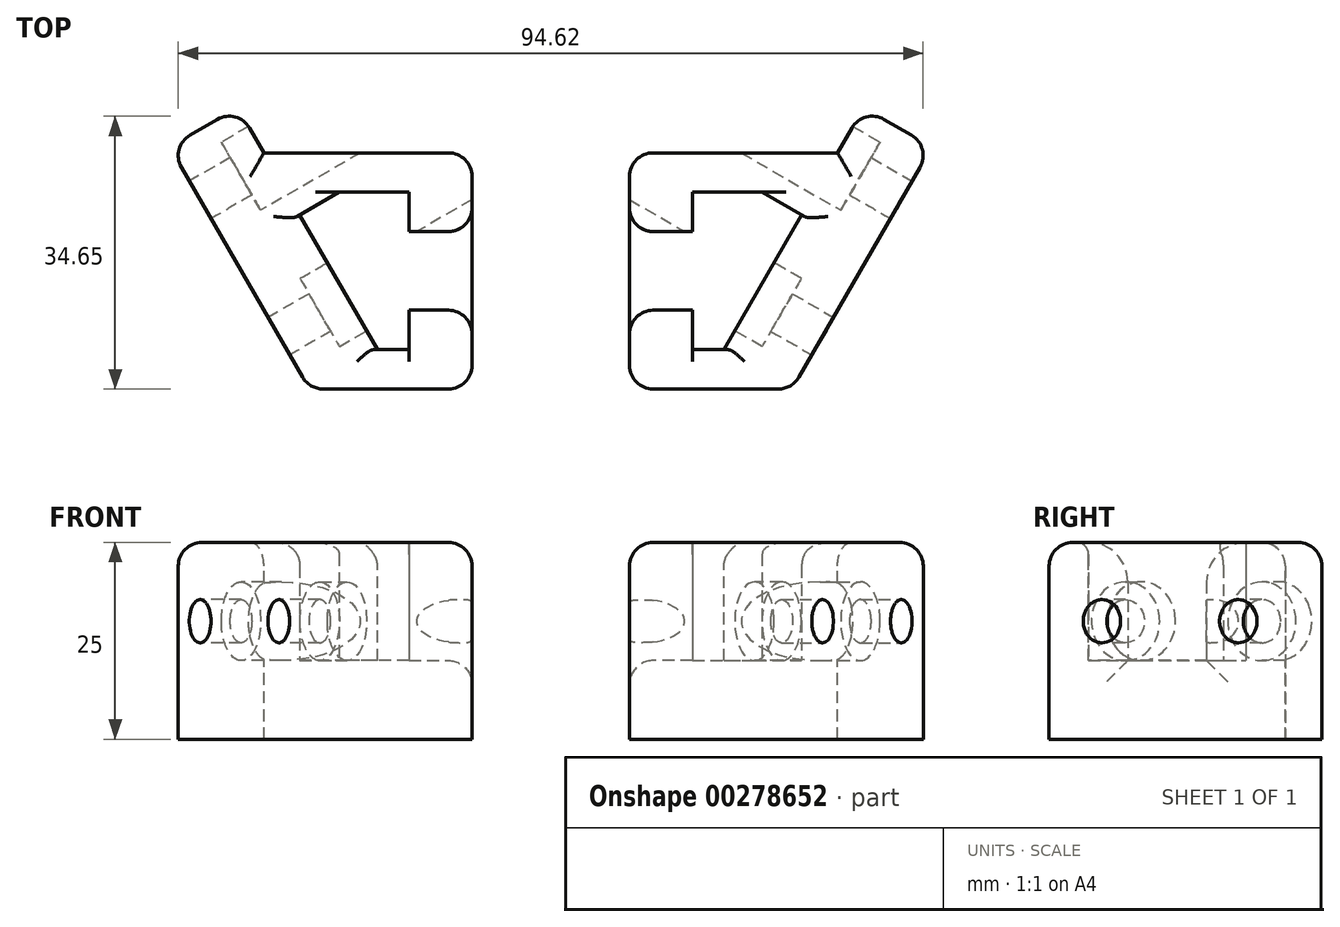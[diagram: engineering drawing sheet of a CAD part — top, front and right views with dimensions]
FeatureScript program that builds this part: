
annotation { "Feature Type Name" : "Feature", "Feature Type Description" : "" }
export const myFeature = defineFeature(function(context is Context, id is Id, definition is map)
    precondition{}
    {
        {
            var Q0;
            Q0=qCreatedBy(makeId("Top.planeOp"),FACE);
            var sketch = newSketch(context, id + "F0", { "sketchPlane" : qUnion([Q0])});
            skLineSegment(sketch, "E0.bottom", {"start": v(-4, 10) * mm, "end": v(4, 10) * mm});
            skLineSegment(sketch, "E0.top", {"start": v(-4, -10) * mm, "end": v(4, -10) * mm});
            skLineSegment(sketch, "E0.left", {"start": v(-4, 10) * mm, "end": v(-4, -10) * mm});
            skLineSegment(sketch, "E0.right", {"start": v(4, 10) * mm, "end": v(4, -10) * mm});
            skPoint(sketch, "E1", {"position": v(0, 10) * mm});
            skPoint(sketch, "E2", {"position": v(4, 0) * mm});
            skLineSegment(sketch, "E3.bottom", {"start": v(-4, 5) * mm, "end": v(4, 5) * mm});
            skLineSegment(sketch, "E3.top", {"start": v(-4, -5) * mm, "end": v(4, -5) * mm});
            skLineSegment(sketch, "E3.left", {"start": v(-4, 5) * mm, "end": v(-4, -5) * mm});
            skLineSegment(sketch, "E3.right", {"start": v(4, 5) * mm, "end": v(4, -5) * mm});
            skPoint(sketch, "E4", {"position": v(-4, 0) * mm});
            skSolve(sketch);
        }
        {
            var Q0;
            {var subQ0=sQuery(id+"F0.wireOp",EDGE,"E0.bottom");Q0=makeQuery(id+"F0.imprint","IMPRINT",FACE,{"disambiguationData":[TD([[makeQuery(id+"F0.imprint","IMPRINT",EDGE,{"derivedFrom":subQ0}),-1.0]])]});}
            var Q1;
            {var subQ0=sQuery(id+"F0.wireOp",EDGE,"E0.top");Q1=makeQuery(id+"F0.imprint","IMPRINT",FACE,{"disambiguationData":[TD([[makeQuery(id+"F0.imprint","IMPRINT",EDGE,{"derivedFrom":subQ0}),1.0]])]});}
            extrude(context, id + "F1", {"entities" : qUnion([Q0, Q1]), "depth" : 25 * mm});
        }
        {
            var Q0;
            Q0=makeQuery(id+"F1.opExtrude","CAP_FACE",FACE,{"disambiguationData":[OSD([sQuery(id+"F0.wireOp",EDGE,"E0.top"),sQuery(id+"F0.wireOp",EDGE,"E0.left"),sQuery(id+"F0.wireOp",EDGE,"E0.right"),sQuery(id+"F0.wireOp",EDGE,"E3.top")])],"isStart":true});
            var sketch = newSketch(context, id + "F2", { "sketchPlane" : qUnion([Q0])});
            skLineSegment(sketch, "E5.bottom", {"start": v(4, -10) * mm, "end": v(-8, -10) * mm});
            skLineSegment(sketch, "E5.top", {"start": v(4, 10) * mm, "end": v(-8, 10) * mm});
            skLineSegment(sketch, "E5.left", {"start": v(4, -10) * mm, "end": v(4, 10) * mm});
            skLineSegment(sketch, "E5.right", {"start": v(-8, -10) * mm, "end": v(-8, 10) * mm});
            skLineSegment(sketch, "E6", {"start": v(-8, 10) * mm, "end": v(-19.55, -10) * mm});
            skLineSegment(sketch, "E7", {"start": v(-8, -10) * mm, "end": v(-19.55, -10) * mm});
            skSolve(sketch);
        }
        {
            var Q0;
            {var subQ4=sQuery(id+"F2.wireOp",EDGE,"E5.bottom");Q0=makeQuery(id+"F2.imprint","IMPRINT",FACE,{"disambiguationData":[TD([[makeQuery(id+"F2.imprint","IMPRINT",EDGE,{"derivedFrom":subQ4}),-1.0]])]});}
            var Q1;
            Q1=makeQuery(id+"F2.imprint","IMPRINT",FACE,{"disambiguationData":[TD([[makeQuery(id+"F2.imprint","IMPRINT",EDGE,{"derivedFrom":sQuery(id+"F2.wireOp",EDGE,"E5.right")}),1.0]])]});
            extrude(context, id + "F3", {"entities" : qUnion([Q0, Q1]), "oppositeDirection" : true, "depth" : 10 * mm});
        }
        {
            var Q0;
            Q0=makeQuery(id+"F3.opExtrude","SWEPT_FACE",FACE,{"disambiguationData":[OSD([sQuery(id+"F2.wireOp",EDGE,"E6")])]});
            var sketch = newSketch(context, id + "F4", { "sketchPlane" : qUnion([Q0])});
            skLineSegment(sketch, "E8.bottom", {"start": v(4.66, 0) * mm, "end": v(-18.43, 0) * mm});
            skLineSegment(sketch, "E8.top", {"start": v(4.66, 25) * mm, "end": v(-18.43, 25) * mm});
            skLineSegment(sketch, "E8.left", {"start": v(4.66, 0) * mm, "end": v(4.66, 25) * mm});
            skLineSegment(sketch, "E8.right", {"start": v(-18.43, 0) * mm, "end": v(-18.43, 25) * mm});
            skSolve(sketch);
        }
        {
            var Q0;
            {var subQ0=sQuery(id+"F4.wireOp",EDGE,"E8.top");Q0=makeQuery(id+"F4.imprint","IMPRINT",FACE,{"disambiguationData":[TD([[makeQuery(id+"F4.imprint","IMPRINT",EDGE,{"derivedFrom":subQ0}),1.0]])]});}
            var Q1;
            {var subQ0=sQuery(id+"F4.wireOp",EDGE,"E8.bottom");Q1=makeQuery(id+"F4.imprint","IMPRINT",FACE,{"disambiguationData":[TD([[makeQuery(id+"F4.imprint","IMPRINT",EDGE,{"derivedFrom":subQ0}),-1.0]])]});}
            extrude(context, id + "F5", {"entities" : qUnion([Q0, Q1]), "operationType" : NewBodyOperationType.ADD, "depth" : 10 * mm});
        }
        {
            var Q0;
            Q0=makeQuery(id+"F1.opExtrude","SWEPT_FACE",FACE,{"disambiguationData":[OSD([sQuery(id+"F0.wireOp",EDGE,"E0.top")])]});
            var sketch = newSketch(context, id + "F6", { "sketchPlane" : qUnion([Q0])});
            skLineSegment(sketch, "E9.bottom", {"start": v(4, 25) * mm, "end": v(-16.66, 25) * mm});
            skLineSegment(sketch, "E9.top", {"start": v(4, 0) * mm, "end": v(-16.66, 0) * mm});
            skLineSegment(sketch, "E9.left", {"start": v(4, 25) * mm, "end": v(4, 0) * mm});
            skLineSegment(sketch, "E9.right", {"start": v(-16.66, 25) * mm, "end": v(-16.66, 0) * mm});
            skSolve(sketch);
        }
        {
            var Q0;
            {var subQ2=sQuery(id+"F6.wireOp",EDGE,"E9.right");Q0=makeQuery(id+"F6.imprint","IMPRINT",FACE,{"disambiguationData":[TD([[makeQuery(id+"F6.imprint","IMPRINT",EDGE,{"derivedFrom":subQ2}),1.0]])]});}
            var Q1;
            {var subQ2=sQuery(id+"F6.wireOp",EDGE,"E9.left");Q1=makeQuery(id+"F6.imprint","IMPRINT",FACE,{"disambiguationData":[TD([[makeQuery(id+"F6.imprint","IMPRINT",EDGE,{"derivedFrom":subQ2}),-1.0]])]});}
            extrude(context, id + "F7", {"entities" : qUnion([Q0, Q1]), "depth" : 2.5 * mm});
        }
        {
            var Q0;
            Q0=makeQuery(id+"F1.opExtrude","SWEPT_FACE",FACE,{"disambiguationData":[OSD([sQuery(id+"F0.wireOp",EDGE,"E0.bottom")])]});
            var sketch = newSketch(context, id + "F8", { "sketchPlane" : qUnion([Q0])});
            skLineSegment(sketch, "E10.bottom", {"start": v(-4, 25) * mm, "end": v(28.2, 25) * mm});
            skLineSegment(sketch, "E10.top", {"start": v(-4, 0) * mm, "end": v(28.2, 0) * mm});
            skLineSegment(sketch, "E10.left", {"start": v(-4, 25) * mm, "end": v(-4, 0) * mm});
            skLineSegment(sketch, "E10.right", {"start": v(28.2, 25) * mm, "end": v(28.2, 0) * mm});
            skSolve(sketch);
        }
        {
            var Q0;
            {var subQ2=sQuery(id+"F8.wireOp",EDGE,"E10.right");Q0=makeQuery(id+"F8.imprint","IMPRINT",FACE,{"disambiguationData":[TD([[makeQuery(id+"F8.imprint","IMPRINT",EDGE,{"derivedFrom":subQ2}),-1.0]])]});}
            var Q1;
            {var subQ2=sQuery(id+"F8.wireOp",EDGE,"E10.left");Q1=makeQuery(id+"F8.imprint","IMPRINT",FACE,{"disambiguationData":[TD([[makeQuery(id+"F8.imprint","IMPRINT",EDGE,{"derivedFrom":subQ2}),1.0]])]});}
            extrude(context, id + "F9", {"entities" : qUnion([Q0, Q1]), "depth" : 5 * mm});
        }
        {
            var Q0;
            Q0=makeQuery(id+"F9.opExtrude","SWEPT_FACE",FACE,{"disambiguationData":[OSD([sQuery(id+"F8.wireOp",EDGE,"E10.bottom")])]});
            var sketch = newSketch(context, id + "F10", { "sketchPlane" : qUnion([Q0])});
            skLineSegment(sketch, "E11", {"start": v(-28.2, 10) * mm, "end": v(-28.2, 5) * mm});
            skLineSegment(sketch, "E12", {"start": v(-28.2, 5) * mm, "end": v(-19.55, 10) * mm});
            skLineSegment(sketch, "E13", {"start": v(-19.55, 10) * mm, "end": v(-28.2, 10) * mm});
            skSolve(sketch);
        }
        {
            var Q0;
            Q0=makeQuery(id+"F10.imprint","IMPRINT",FACE,{"disambiguationData":[TD([[makeQuery(id+"F10.imprint","IMPRINT",EDGE,{"derivedFrom":sQuery(id+"F10.wireOp",EDGE,"E11")}),1.0]])]});
            var Q1;
            Q1=makeQuery(id+"F9.opExtrude","SWEPT_FACE",FACE,{"disambiguationData":[OSD([sQuery(id+"F8.wireOp",EDGE,"E10.top")])]});
            extrude(context, id + "F11", {"entities" : qUnion([Q0]), "endBound" : BoundingType.UP_TO_SURFACE, "oppositeDirection" : true, "endBoundEntityFace" : qUnion([Q1]), "depth" : 25 * mm});
        }
        {
            var Q0;
            Q0=makeQuery(id+"F1.opExtrude","SWEPT_BODY",BODY,{"disambiguationData":[OSD([sQuery(id+"F0.wireOp",EDGE,"E0.bottom"),sQuery(id+"F0.wireOp",EDGE,"E0.left"),sQuery(id+"F0.wireOp",EDGE,"E0.right"),sQuery(id+"F0.wireOp",EDGE,"E3.bottom")])]});
            var Q1;
            Q1=makeQuery(id+"F1.opExtrude","SWEPT_BODY",BODY,{"disambiguationData":[OSD([sQuery(id+"F0.wireOp",EDGE,"E0.top"),sQuery(id+"F0.wireOp",EDGE,"E0.left"),sQuery(id+"F0.wireOp",EDGE,"E0.right"),sQuery(id+"F0.wireOp",EDGE,"E3.top")])]});
            var Q2;
            Q2=makeQuery(id+"F3.opExtrude","SWEPT_BODY",BODY,{"disambiguationData":[OSD([sQuery(id+"F0.wireOp",EDGE,"E0.left"),sQuery(id+"F0.wireOp",EDGE,"E3.top"),sQuery(id+"F2.wireOp",EDGE,"E5.bottom"),sQuery(id+"F2.wireOp",EDGE,"E5.top"),sQuery(id+"F2.wireOp",EDGE,"E5.left"),sQuery(id+"F2.wireOp",EDGE,"E6"),sQuery(id+"F2.wireOp",EDGE,"E7")])]});
            var Q3;
            Q3=makeQuery(id+"F7.opExtrude","SWEPT_BODY",BODY,{"disambiguationData":[OSD([sQuery(id+"F6.wireOp",EDGE,"E9.bottom"),sQuery(id+"F6.wireOp",EDGE,"E9.top"),sQuery(id+"F6.wireOp",EDGE,"E9.left"),sQuery(id+"F6.wireOp",EDGE,"E9.right")])]});
            var Q4;
            Q4=makeQuery(id+"F9.opExtrude","SWEPT_BODY",BODY,{"disambiguationData":[OSD([sQuery(id+"F8.wireOp",EDGE,"E10.bottom"),sQuery(id+"F8.wireOp",EDGE,"E10.top"),sQuery(id+"F8.wireOp",EDGE,"E10.left"),sQuery(id+"F8.wireOp",EDGE,"E10.right")])]});
            var Q5;
            Q5=makeQuery(id+"F11.opExtrude","SWEPT_BODY",BODY,{"disambiguationData":[OSD([sQuery(id+"F10.wireOp",EDGE,"E11"),sQuery(id+"F10.wireOp",EDGE,"E12"),sQuery(id+"F10.wireOp",EDGE,"E13")])]});
            booleanBodies(context, id + "F12", {"operationType" : BooleanOperationType.UNION, "tools" : qUnion([Q0, Q1, Q2, Q3, Q4, Q5])});
        }
        {
            var Q0;
            {var subQ0=sQuery(id+"F0.wireOp",EDGE,"E0.right");var subQ1=sQuery(id+"F0.wireOp",EDGE,"E0.left");Q0=makeQuery(id+"F12.opBoolean","MERGE",FACE,{"derivedFrom":[makeQuery(id+"F1.opExtrude","CAP_FACE",FACE,{"disambiguationData":[OSD([sQuery(id+"F0.wireOp",EDGE,"E0.bottom"),subQ1,subQ0,sQuery(id+"F0.wireOp",EDGE,"E3.bottom")])],"isStart":false}),makeQuery(id+"F1.opExtrude","CAP_FACE",FACE,{"disambiguationData":[OSD([sQuery(id+"F0.wireOp",EDGE,"E0.top"),subQ1,subQ0,sQuery(id+"F0.wireOp",EDGE,"E3.top")])],"isStart":false}),makeQuery(id+"F5.opExtrude","SWEPT_FACE",FACE,{"disambiguationData":[OSD([sQuery(id+"F4.wireOp",EDGE,"E8.top")])]}),makeQuery(id+"F7.opExtrude","SWEPT_FACE",FACE,{"disambiguationData":[OSD([sQuery(id+"F6.wireOp",EDGE,"E9.bottom")])]}),makeQuery(id+"F9.opExtrude","SWEPT_FACE",FACE,{"disambiguationData":[OSD([sQuery(id+"F8.wireOp",EDGE,"E10.bottom")])]}),makeQuery(id+"F11.opExtrude","CAP_FACE",FACE,{"disambiguationData":[OSD([sQuery(id+"F10.wireOp",EDGE,"E11"),sQuery(id+"F10.wireOp",EDGE,"E12"),sQuery(id+"F10.wireOp",EDGE,"E13")])],"isStart":true})]});}
            var sketch = newSketch(context, id + "F13", { "sketchPlane" : qUnion([Q0])});
            skLineSegment(sketch, "E14", {"start": v(-28.2, 5) * mm, "end": v(-32.54, 12.5) * mm});
            skLineSegment(sketch, "E15", {"start": v(-32.54, 12.5) * mm, "end": v(-23.88, 17.5) * mm});
            skLineSegment(sketch, "E16", {"start": v(-23.88, 17.5) * mm, "end": v(-19.55, 10) * mm});
            skLineSegment(sketch, "E17", {"start": v(-28.2, 15) * mm, "end": v(-32.54, 15) * mm});
            skLineSegment(sketch, "E18", {"start": v(-32.54, 15) * mm, "end": v(-32.54, 12.5) * mm});
            skSolve(sketch);
        }
        {
            var Q0;
            {var subQ0=sQuery(id+"F13.wireOp",EDGE,"E14");Q0=makeQuery(id+"F13.imprint","IMPRINT",FACE,{"disambiguationData":[TD([[makeQuery(id+"F13.imprint","IMPRINT",EDGE,{"derivedFrom":subQ0}),-1.0]])]});}
            var Q1;
            {var subQ0=sQuery(id+"F13.wireOp",EDGE,"E17");Q1=makeQuery(id+"F13.imprint","IMPRINT",FACE,{"disambiguationData":[TD([[makeQuery(id+"F13.imprint","IMPRINT",EDGE,{"derivedFrom":subQ0}),1.0]])]});}
            var Q2;
            {var subQ0=sQuery(id+"F0.wireOp",EDGE,"E3.top");var subQ1=sQuery(id+"F0.wireOp",EDGE,"E0.left");var subQ2=sQuery(id+"F0.wireOp",EDGE,"E0.right");Q2=makeQuery(id+"F12.opBoolean","MERGE",FACE,{"derivedFrom":[makeQuery(id+"F1.opExtrude","CAP_FACE",FACE,{"disambiguationData":[OSD([sQuery(id+"F0.wireOp",EDGE,"E0.bottom"),subQ1,subQ2,sQuery(id+"F0.wireOp",EDGE,"E3.bottom")])],"isStart":true}),makeQuery(id+"F1.opExtrude","CAP_FACE",FACE,{"disambiguationData":[OSD([sQuery(id+"F0.wireOp",EDGE,"E0.top"),subQ1,subQ2,subQ0])],"isStart":true}),makeQuery(id+"F5.boolean.opBoolean","MERGE",FACE,{"derivedFrom":[makeQuery(id+"F3.opExtrude","CAP_FACE",FACE,{"disambiguationData":[OSD([subQ1,subQ0,sQuery(id+"F2.wireOp",EDGE,"E5.bottom"),sQuery(id+"F2.wireOp",EDGE,"E5.top"),sQuery(id+"F2.wireOp",EDGE,"E5.left"),sQuery(id+"F2.wireOp",EDGE,"E6"),sQuery(id+"F2.wireOp",EDGE,"E7")])],"isStart":true}),makeQuery(id+"F5.opExtrude","SWEPT_FACE",FACE,{"disambiguationData":[OSD([sQuery(id+"F4.wireOp",EDGE,"E8.bottom")])]})]}),makeQuery(id+"F7.opExtrude","SWEPT_FACE",FACE,{"disambiguationData":[OSD([sQuery(id+"F6.wireOp",EDGE,"E9.top")])]}),makeQuery(id+"F9.opExtrude","SWEPT_FACE",FACE,{"disambiguationData":[OSD([sQuery(id+"F8.wireOp",EDGE,"E10.top")])]}),makeQuery(id+"F11.opExtrude","CAP_FACE",FACE,{"disambiguationData":[OSD([sQuery(id+"F10.wireOp",EDGE,"E11"),sQuery(id+"F10.wireOp",EDGE,"E12"),sQuery(id+"F10.wireOp",EDGE,"E13")])],"isStart":false})]});}
            extrude(context, id + "F14", {"entities" : qUnion([Q0, Q1]), "operationType" : NewBodyOperationType.ADD, "endBound" : BoundingType.UP_TO_SURFACE, "oppositeDirection" : true, "endBoundEntityFace" : qUnion([Q2]), "depth" : 25 * mm});
        }
        {
            var Q0;
            {var subQ0=sQuery(id+"F10.wireOp",EDGE,"E11");var subQ1=sQuery(id+"F8.wireOp",EDGE,"E10.bottom");var subQ2=sQuery(id+"F0.wireOp",EDGE,"E0.right");var subQ3=sQuery(id+"F0.wireOp",EDGE,"E0.left");Q0=makeQuery(id+"F14.boolean.opBoolean","MERGE",FACE,{"derivedFrom":[makeQuery(id+"F12.opBoolean","MERGE",FACE,{"derivedFrom":[makeQuery(id+"F1.opExtrude","CAP_FACE",FACE,{"disambiguationData":[OSD([sQuery(id+"F0.wireOp",EDGE,"E0.bottom"),subQ3,subQ2,sQuery(id+"F0.wireOp",EDGE,"E3.bottom")])],"isStart":false}),makeQuery(id+"F1.opExtrude","CAP_FACE",FACE,{"disambiguationData":[OSD([sQuery(id+"F0.wireOp",EDGE,"E0.top"),subQ3,subQ2,sQuery(id+"F0.wireOp",EDGE,"E3.top")])],"isStart":false}),makeQuery(id+"F5.opExtrude","SWEPT_FACE",FACE,{"disambiguationData":[OSD([sQuery(id+"F4.wireOp",EDGE,"E8.top")])]}),makeQuery(id+"F7.opExtrude","SWEPT_FACE",FACE,{"disambiguationData":[OSD([sQuery(id+"F6.wireOp",EDGE,"E9.bottom")])]}),makeQuery(id+"F9.opExtrude","SWEPT_FACE",FACE,{"disambiguationData":[OSD([subQ1])]}),makeQuery(id+"F11.opExtrude","CAP_FACE",FACE,{"disambiguationData":[OSD([subQ0,sQuery(id+"F10.wireOp",EDGE,"E12"),sQuery(id+"F10.wireOp",EDGE,"E13")])],"isStart":true})]}),makeQuery(id+"F14.opExtrude","CAP_FACE",FACE,{"disambiguationData":[OSD([subQ1,sQuery(id+"F8.wireOp",EDGE,"E10.right"),subQ0,sQuery(id+"F13.wireOp",EDGE,"E14"),sQuery(id+"F13.wireOp",EDGE,"E17"),sQuery(id+"F13.wireOp",EDGE,"E18")])],"isStart":true})]});}
            var sketch = newSketch(context, id + "F15", { "sketchPlane" : qUnion([Q0])});
            skLineSegment(sketch, "E19", {"start": v(-16.66, -15) * mm, "end": v(4, -15) * mm});
            skLineSegment(sketch, "E20", {"start": v(4, -15) * mm, "end": v(4, -12.5) * mm});
            skLineSegment(sketch, "E21", {"start": v(-16.66, -15) * mm, "end": v(-12.33, -12.5) * mm});
            skLineSegment(sketch, "E22", {"start": v(-12.33, -12.5) * mm, "end": v(4, -12.5) * mm});
            skSolve(sketch);
        }
        {
            var Q0;
            Q0=qSketchRegion(id+"F15",true);
            var Q1;
            {var subQ0=sQuery(id+"F10.wireOp",EDGE,"E11");var subQ1=sQuery(id+"F0.wireOp",EDGE,"E3.top");var subQ2=sQuery(id+"F0.wireOp",EDGE,"E0.left");var subQ3=sQuery(id+"F0.wireOp",EDGE,"E0.right");Q1=makeQuery(id+"F14.boolean.opBoolean","MERGE",FACE,{"derivedFrom":[makeQuery(id+"F12.opBoolean","MERGE",FACE,{"derivedFrom":[makeQuery(id+"F1.opExtrude","CAP_FACE",FACE,{"disambiguationData":[OSD([sQuery(id+"F0.wireOp",EDGE,"E0.bottom"),subQ2,subQ3,sQuery(id+"F0.wireOp",EDGE,"E3.bottom")])],"isStart":true}),makeQuery(id+"F1.opExtrude","CAP_FACE",FACE,{"disambiguationData":[OSD([sQuery(id+"F0.wireOp",EDGE,"E0.top"),subQ2,subQ3,subQ1])],"isStart":true}),makeQuery(id+"F5.boolean.opBoolean","MERGE",FACE,{"derivedFrom":[makeQuery(id+"F3.opExtrude","CAP_FACE",FACE,{"disambiguationData":[OSD([subQ2,subQ1,sQuery(id+"F2.wireOp",EDGE,"E5.bottom"),sQuery(id+"F2.wireOp",EDGE,"E5.top"),sQuery(id+"F2.wireOp",EDGE,"E5.left"),sQuery(id+"F2.wireOp",EDGE,"E6"),sQuery(id+"F2.wireOp",EDGE,"E7")])],"isStart":true}),makeQuery(id+"F5.opExtrude","SWEPT_FACE",FACE,{"disambiguationData":[OSD([sQuery(id+"F4.wireOp",EDGE,"E8.bottom")])]})]}),makeQuery(id+"F7.opExtrude","SWEPT_FACE",FACE,{"disambiguationData":[OSD([sQuery(id+"F6.wireOp",EDGE,"E9.top")])]}),makeQuery(id+"F9.opExtrude","SWEPT_FACE",FACE,{"disambiguationData":[OSD([sQuery(id+"F8.wireOp",EDGE,"E10.top")])]}),makeQuery(id+"F11.opExtrude","CAP_FACE",FACE,{"disambiguationData":[OSD([subQ0,sQuery(id+"F10.wireOp",EDGE,"E12"),sQuery(id+"F10.wireOp",EDGE,"E13")])],"isStart":false})]}),makeQuery(id+"F14.opExtrude","CAP_FACE",FACE,{"disambiguationData":[OSD([sQuery(id+"F8.wireOp",EDGE,"E10.bottom"),sQuery(id+"F8.wireOp",EDGE,"E10.right"),subQ0,sQuery(id+"F13.wireOp",EDGE,"E14"),sQuery(id+"F13.wireOp",EDGE,"E17"),sQuery(id+"F13.wireOp",EDGE,"E18")])],"isStart":false})]});}
            extrude(context, id + "F16", {"entities" : qUnion([Q0]), "operationType" : NewBodyOperationType.ADD, "endBound" : BoundingType.UP_TO_SURFACE, "oppositeDirection" : true, "endBoundEntityFace" : qUnion([Q1]), "depth" : 25 * mm});
        }
        {
            var Q0;
            Q0=makeQuery(id+"F14.boolean.opBoolean","MERGE",FACE,{"derivedFrom":[makeQuery(id+"F5.opExtrude","CAP_FACE",FACE,{"disambiguationData":[OSD([sQuery(id+"F4.wireOp",EDGE,"E8.bottom"),sQuery(id+"F4.wireOp",EDGE,"E8.top"),sQuery(id+"F4.wireOp",EDGE,"E8.left"),sQuery(id+"F4.wireOp",EDGE,"E8.right")])],"isStart":false}),makeQuery(id+"F14.opExtrude","SWEPT_FACE",FACE,{"disambiguationData":[OSD([sQuery(id+"F13.wireOp",EDGE,"E14")])]})]});
            var sketch = newSketch(context, id + "F17", { "sketchPlane" : qUnion([Q0])});
            skCircle(sketch, "E23", {"center": v(-23.09, 15) * mm, "radius": 2.75 * mm});
            skCircle(sketch, "E24", {"center": v(-3.09, 15) * mm, "radius": 2.75 * mm});
            skLineSegment(sketch, "E25", {"start": v(-23.09, 15) * mm, "end": v(-3.09, 15) * mm});
            skPoint(sketch, "E26", {"position": v(-13.09, 15) * mm});
            skLineSegment(sketch, "E27.bottom", {"start": v(-30.84, 25) * mm, "end": v(4.66, 25) * mm});
            skLineSegment(sketch, "E27.top", {"start": v(-30.84, 0) * mm, "end": v(4.66, 0) * mm});
            skLineSegment(sketch, "E27.left", {"start": v(-30.84, 25) * mm, "end": v(-30.84, 0) * mm});
            skLineSegment(sketch, "E27.right", {"start": v(4.66, 25) * mm, "end": v(4.66, 0) * mm});
            skPoint(sketch, "E28", {"position": v(-11.22, 25) * mm});
            skSolve(sketch);
        }
        {
            var Q0;
            Q0=makeQuery(id+"F17.imprint","IMPRINT",FACE,{"disambiguationData":[TD([[makeQuery(id+"F17.imprint","IMPRINT",EDGE,{"derivedFrom":sQuery(id+"F17.wireOp",EDGE,"E24")}),-1.0]])]});
            var Q1;
            {var subQ0=sQuery(id+"F17.wireOp",EDGE,"E27.left");Q1=makeQuery(id+"F17.imprint","IMPRINT",FACE,{"disambiguationData":[TD([[makeQuery(id+"F17.imprint","IMPRINT",EDGE,{"derivedFrom":subQ0}),1.0]])]});}
            extrude(context, id + "F18", {"entities" : qUnion([Q0, Q1]), "operationType" : NewBodyOperationType.ADD, "oppositeDirection" : true, "depth" : 10 * mm});
        }
        {
            var Q0;
            Q0=makeQuery(id+"F18.boolean.opBoolean","MERGE",FACE,{"derivedFrom":[makeQuery(id+"F14.boolean.opBoolean","MERGE",FACE,{"derivedFrom":[makeQuery(id+"F5.opExtrude","CAP_FACE",FACE,{"disambiguationData":[OSD([sQuery(id+"F4.wireOp",EDGE,"E8.bottom"),sQuery(id+"F4.wireOp",EDGE,"E8.top"),sQuery(id+"F4.wireOp",EDGE,"E8.left"),sQuery(id+"F4.wireOp",EDGE,"E8.right")])],"isStart":false}),makeQuery(id+"F14.opExtrude","SWEPT_FACE",FACE,{"disambiguationData":[OSD([sQuery(id+"F13.wireOp",EDGE,"E14")])]})]}),makeQuery(id+"F18.opExtrude","CAP_FACE",FACE,{"disambiguationData":[OSD([sQuery(id+"F17.wireOp",EDGE,"E23"),sQuery(id+"F17.wireOp",EDGE,"E24"),sQuery(id+"F17.wireOp",EDGE,"E27.bottom"),sQuery(id+"F17.wireOp",EDGE,"E27.top"),sQuery(id+"F17.wireOp",EDGE,"E27.left"),sQuery(id+"F17.wireOp",EDGE,"E27.right")])],"isStart":true})]});
            var sketch = newSketch(context, id + "F19", { "sketchPlane" : qUnion([Q0])});
            skCircle(sketch, "E29", {"center": v(-3.09, 15) * mm, "radius": 2.75 * mm});
            skCircle(sketch, "E30", {"center": v(-23.09, 15) * mm, "radius": 2.75 * mm});
            skSolve(sketch);
        }
        {
            var Q0;
            Q0=makeQuery(id+"F19.imprint","IMPRINT",FACE,{"disambiguationData":[TD([[makeQuery(id+"F19.imprint","IMPRINT",EDGE,{"derivedFrom":sQuery(id+"F19.wireOp",EDGE,"E29")}),1.0]])]});
            var Q1;
            {var subQ1=makeQuery(id+"F14.opExtrude","SWEPT_EDGE",EDGE,{"disambiguationData":[OSD([sQuery(id+"F13.wireOp",EDGE,"E14"),sQuery(id+"F13.wireOp",EDGE,"E15"),sQuery(id+"F13.wireOp",EDGE,"E18")])]});Q1=makeQuery(id+"F19.imprint","IMPRINT",FACE,{"disambiguationData":[TD([[makeQuery(id+"F19.imprint","IMPRINT",EDGE,{"derivedFrom":subQ1}),-1.0]])]});}
            var Q2;
            {var subQ1=makeQuery(id+"F14.opExtrude","SWEPT_EDGE",EDGE,{"disambiguationData":[OSD([sQuery(id+"F13.wireOp",EDGE,"E14"),sQuery(id+"F13.wireOp",EDGE,"E15"),sQuery(id+"F13.wireOp",EDGE,"E18")])]});Q2=makeQuery(id+"F19.imprint","IMPRINT",FACE,{"disambiguationData":[TD([[makeQuery(id+"F19.imprint","IMPRINT",EDGE,{"derivedFrom":subQ1}),1.0]])]});}
            var Q3;
            Q3=makeQuery(id+"F19.imprint","IMPRINT",FACE,{"disambiguationData":[TD([[makeQuery(id+"F19.imprint","IMPRINT",EDGE,{"derivedFrom":sQuery(id+"F19.wireOp",EDGE,"E30")}),1.0]])]});
            extrude(context, id + "F20", {"entities" : qUnion([Q0, Q1, Q2, Q3]), "operationType" : NewBodyOperationType.REMOVE, "endBound" : BoundingType.THROUGH_ALL, "oppositeDirection" : true, "depth" : 25 * mm});
        }
        {
            var Q0;
            Q0=makeQuery(id+"F3.opExtrude","CAP_FACE",FACE,{"disambiguationData":[OSD([sQuery(id+"F0.wireOp",EDGE,"E0.left"),sQuery(id+"F0.wireOp",EDGE,"E3.top"),sQuery(id+"F2.wireOp",EDGE,"E5.bottom"),sQuery(id+"F2.wireOp",EDGE,"E5.top"),sQuery(id+"F2.wireOp",EDGE,"E5.left"),sQuery(id+"F2.wireOp",EDGE,"E6"),sQuery(id+"F2.wireOp",EDGE,"E7")])],"isStart":false});
            var sketch = newSketch(context, id + "F21", { "sketchPlane" : qUnion([Q0])});
            skLineSegment(sketch, "E31", {"start": v(-17.87, 7.1) * mm, "end": v(-12.86, 10) * mm});
            skSolve(sketch);
        }
        {
            var Q0;
            {var subQ0=sQuery(id+"F21.wireOp",EDGE,"E31");Q0=makeQuery(id+"F21.imprint","IMPRINT",FACE,{"disambiguationData":[TD([[makeQuery(id+"F21.imprint","IMPRINT",EDGE,{"derivedFrom":subQ0}),1.0]])]});}
            var Q1;
            {var subQ0=sQuery(id+"F10.wireOp",EDGE,"E11");var subQ1=sQuery(id+"F8.wireOp",EDGE,"E10.bottom");var subQ2=sQuery(id+"F0.wireOp",EDGE,"E0.right");var subQ3=sQuery(id+"F0.wireOp",EDGE,"E0.left");Q1=makeQuery(id+"F18.boolean.opBoolean","MERGE",FACE,{"derivedFrom":[makeQuery(id+"F16.boolean.opBoolean","MERGE",FACE,{"derivedFrom":[makeQuery(id+"F14.boolean.opBoolean","MERGE",FACE,{"derivedFrom":[makeQuery(id+"F12.opBoolean","MERGE",FACE,{"derivedFrom":[makeQuery(id+"F1.opExtrude","CAP_FACE",FACE,{"disambiguationData":[OSD([sQuery(id+"F0.wireOp",EDGE,"E0.bottom"),subQ3,subQ2,sQuery(id+"F0.wireOp",EDGE,"E3.bottom")])],"isStart":false}),makeQuery(id+"F1.opExtrude","CAP_FACE",FACE,{"disambiguationData":[OSD([sQuery(id+"F0.wireOp",EDGE,"E0.top"),subQ3,subQ2,sQuery(id+"F0.wireOp",EDGE,"E3.top")])],"isStart":false}),makeQuery(id+"F5.opExtrude","SWEPT_FACE",FACE,{"disambiguationData":[OSD([sQuery(id+"F4.wireOp",EDGE,"E8.top")])]}),makeQuery(id+"F7.opExtrude","SWEPT_FACE",FACE,{"disambiguationData":[OSD([sQuery(id+"F6.wireOp",EDGE,"E9.bottom")])]}),makeQuery(id+"F9.opExtrude","SWEPT_FACE",FACE,{"disambiguationData":[OSD([subQ1])]}),makeQuery(id+"F11.opExtrude","CAP_FACE",FACE,{"disambiguationData":[OSD([subQ0,sQuery(id+"F10.wireOp",EDGE,"E12"),sQuery(id+"F10.wireOp",EDGE,"E13")])],"isStart":true})]}),makeQuery(id+"F14.opExtrude","CAP_FACE",FACE,{"disambiguationData":[OSD([subQ1,sQuery(id+"F8.wireOp",EDGE,"E10.right"),subQ0,sQuery(id+"F13.wireOp",EDGE,"E14"),sQuery(id+"F13.wireOp",EDGE,"E17"),sQuery(id+"F13.wireOp",EDGE,"E18")])],"isStart":true})]}),makeQuery(id+"F16.opExtrude","CAP_FACE",FACE,{"disambiguationData":[OSD([sQuery(id+"F15.wireOp",EDGE,"E19"),sQuery(id+"F15.wireOp",EDGE,"E20"),sQuery(id+"F15.wireOp",EDGE,"E21"),sQuery(id+"F15.wireOp",EDGE,"E22")])],"isStart":true})]}),makeQuery(id+"F18.opExtrude","SWEPT_FACE",FACE,{"disambiguationData":[OSD([sQuery(id+"F17.wireOp",EDGE,"E27.bottom")])]})]});}
            extrude(context, id + "F22", {"entities" : qUnion([Q0]), "operationType" : NewBodyOperationType.ADD, "endBound" : BoundingType.UP_TO_SURFACE, "endBoundEntityFace" : qUnion([Q1]), "depth" : 25 * mm});
        }
        {
            var Q0;
            Q0=makeQuery(id+"F18.opExtrude","CAP_FACE",FACE,{"disambiguationData":[OSD([sQuery(id+"F17.wireOp",EDGE,"E23"),sQuery(id+"F17.wireOp",EDGE,"E24"),sQuery(id+"F17.wireOp",EDGE,"E27.bottom"),sQuery(id+"F17.wireOp",EDGE,"E27.top"),sQuery(id+"F17.wireOp",EDGE,"E27.left"),sQuery(id+"F17.wireOp",EDGE,"E27.right")])],"isStart":false});
            var sketch = newSketch(context, id + "F23", { "sketchPlane" : qUnion([Q0])});
            skCircle(sketch, "E32", {"center": v(23.09, 15) * mm, "radius": 5 * mm});
            skSolve(sketch);
        }
        {
            var Q0;
            {var subQ1=sQuery(id+"F17.wireOp",EDGE,"E23");Q0=makeQuery(id+"F23.imprint","IMPRINT",FACE,{"disambiguationData":[TD([[makeQuery(id+"F23.imprint","IMPRINT",EDGE,{"derivedFrom":makeQuery(id+"F18.opExtrude","CAP_EDGE",EDGE,{"disambiguationData":[OSD([subQ1])],"isStart":false})}),1.0]])]});}
            var Q1;
            {var subQ1=sQuery(id+"F17.wireOp",EDGE,"E23");var subQ8=makeQuery(id+"F18.opExtrude","CAP_EDGE",EDGE,{"disambiguationData":[OSD([subQ1])],"isStart":false});var subQ9=makeQuery(id+"F23.imprint","IMPRINT",EDGE,{"derivedFrom":subQ8});Q1=qUnion([makeQuery(id+"F23.imprint","IMPRINT",FACE,{"disambiguationData":[TD([[subQ9,-1.0]])]}),makeQuery(id+"F23.imprint","IMPRINT",FACE,{"disambiguationData":[TD([[subQ9,1.0]])]})]);}
            extrude(context, id + "F24", {"entities" : qUnion([Q0, Q1]), "operationType" : NewBodyOperationType.REMOVE, "depth" : 25 * mm});
        }
        {
            var Q0;
            Q0=makeQuery(id+"F5.opExtrude","CAP_FACE",FACE,{"disambiguationData":[OSD([sQuery(id+"F4.wireOp",EDGE,"E8.bottom"),sQuery(id+"F4.wireOp",EDGE,"E8.top"),sQuery(id+"F4.wireOp",EDGE,"E8.left"),sQuery(id+"F4.wireOp",EDGE,"E8.right")])],"isStart":true});
            var sketch = newSketch(context, id + "F25", { "sketchPlane" : qUnion([Q0])});
            skCircle(sketch, "E33", {"center": v(3.09, 15) * mm, "radius": 5 * mm});
            skCircle(sketch, "E34", {"center": v(23.09, 15) * mm, "radius": 5 * mm});
            skSolve(sketch);
        }
        {
            var Q0;
            Q0=makeQuery(id+"F25.imprint","IMPRINT",FACE,{"disambiguationData":[TD([[makeQuery(id+"F25.imprint","IMPRINT",EDGE,{"derivedFrom":sQuery(id+"F25.wireOp",EDGE,"E33")}),1.0]])]});
            var Q1;
            Q1=makeQuery(id+"F25.imprint","IMPRINT",FACE,{"disambiguationData":[TD([[makeQuery(id+"F25.imprint","IMPRINT",EDGE,{"derivedFrom":sQuery(id+"F25.wireOp",EDGE,"E34")}),1.0]])]});
            extrude(context, id + "F26", {"entities" : qUnion([Q0, Q1]), "operationType" : NewBodyOperationType.REMOVE, "oppositeDirection" : true, "depth" : 4 * mm});
        }
        {
            var Q0;
            Q0=makeQuery(id+"F1.opExtrude","CAP_EDGE",EDGE,{"disambiguationData":[OSD([sQuery(id+"F0.wireOp",EDGE,"E3.top")])],"isStart":false});
            var Q1;
            Q1=makeQuery(id+"F1.opExtrude","CAP_EDGE",EDGE,{"disambiguationData":[OSD([sQuery(id+"F0.wireOp",EDGE,"E3.bottom")])],"isStart":false});
            fillet(context, id + "F27", {"entities" : qUnion([Q0, Q1]), "radius" : 5 * mm, "tangentPropagation" : true, "allowEdgeOverflow" : false});
        }
        {
            var Q0;
            Q0=makeQuery(id+"F3.opExtrude","CAP_EDGE",EDGE,{"disambiguationData":[OSD([sQuery(id+"F2.wireOp",EDGE,"E5.left")])],"isStart":false});
            var Q1;
            Q1=makeQuery(id+"F1.opExtrude","SWEPT_EDGE",EDGE,{"disambiguationData":[OSD([sQuery(id+"F0.wireOp",EDGE,"E0.right"),sQuery(id+"F0.wireOp",EDGE,"E3.top"),sQuery(id+"F0.wireOp",EDGE,"E3.right")])]});
            var Q2;
            {var subQ0=sQuery(id+"F2.wireOp",EDGE,"E5.left");var subQ1=sQuery(id+"F0.wireOp",EDGE,"E3.top");var subQ2=sQuery(id+"F0.wireOp",EDGE,"E3.bottom");var subQ3=sQuery(id+"F0.wireOp",EDGE,"E0.right");var subQ4=sQuery(id+"F0.wireOp",EDGE,"E3.right");Q2=makeQuery(id+"F20.boolean.opBoolean","SPLIT",EDGE,{"disambiguationData":[TD([makeQuery(id+"F3.opExtrude","CAP_FACE",FACE,{"disambiguationData":[OSD([sQuery(id+"F0.wireOp",EDGE,"E0.left"),subQ1,sQuery(id+"F2.wireOp",EDGE,"E5.bottom"),sQuery(id+"F2.wireOp",EDGE,"E5.top"),subQ0,sQuery(id+"F2.wireOp",EDGE,"E6"),sQuery(id+"F2.wireOp",EDGE,"E7")])],"isStart":false})])],"derivedFrom":makeQuery(id+"F1.opExtrude","SWEPT_EDGE",EDGE,{"disambiguationData":[OSD([subQ3,subQ2,subQ4])]})});}
            var Q3;
            {var subQ2=sQuery(id+"F0.wireOp",EDGE,"E3.bottom");var subQ3=sQuery(id+"F0.wireOp",EDGE,"E0.right");var subQ6=sQuery(id+"F0.wireOp",EDGE,"E3.right");Q3=makeQuery(id+"F20.boolean.opBoolean","SPLIT",EDGE,{"disambiguationData":[TD([makeQuery(id+"F5.opExtrude","SWEPT_FACE",FACE,{"disambiguationData":[OSD([sQuery(id+"F4.wireOp",EDGE,"E8.top")])]})])],"derivedFrom":makeQuery(id+"F1.opExtrude","SWEPT_EDGE",EDGE,{"disambiguationData":[OSD([subQ3,subQ2,subQ6])]})});}
            var Q4;
            Q4=makeQuery(id+"F16.opExtrude","SWEPT_EDGE",EDGE,{"disambiguationData":[OSD([sQuery(id+"F15.wireOp",EDGE,"E19"),sQuery(id+"F15.wireOp",EDGE,"E20")])]});
            var Q5;
            Q5=makeQuery(id+"F9.opExtrude","CAP_EDGE",EDGE,{"disambiguationData":[OSD([sQuery(id+"F8.wireOp",EDGE,"E10.left")])],"isStart":false});
            var Q6;
            Q6=makeQuery(id+"F14.boolean.opBoolean","MERGE",EDGE,{"derivedFrom":[makeQuery(id+"F9.opExtrude","CAP_EDGE",EDGE,{"disambiguationData":[OSD([sQuery(id+"F8.wireOp",EDGE,"E10.bottom")])],"isStart":false}),makeQuery(id+"F14.opExtrude","CAP_EDGE",EDGE,{"disambiguationData":[OSD([sQuery(id+"F13.wireOp",EDGE,"E17")])],"isStart":true})]});
            var Q7;
            Q7=makeQuery(id+"F16.opExtrude","CAP_EDGE",EDGE,{"disambiguationData":[OSD([sQuery(id+"F15.wireOp",EDGE,"E19")])],"isStart":true});
            var Q8;
            Q8=makeQuery(id+"F18.opExtrude","CAP_EDGE",EDGE,{"disambiguationData":[OSD([sQuery(id+"F17.wireOp",EDGE,"E27.left")])],"isStart":false});
            var Q9;
            Q9=makeQuery(id+"F18.opExtrude","CAP_EDGE",EDGE,{"disambiguationData":[OSD([sQuery(id+"F17.wireOp",EDGE,"E27.left")])],"isStart":true});
            var Q10;
            Q10=makeQuery(id+"F16.boolean.opBoolean","MERGE",EDGE,{"derivedFrom":[makeQuery(id+"F5.opExtrude","CAP_EDGE",EDGE,{"disambiguationData":[OSD([sQuery(id+"F4.wireOp",EDGE,"E8.left")])],"isStart":false}),makeQuery(id+"F16.opExtrude","SWEPT_EDGE",EDGE,{"disambiguationData":[OSD([sQuery(id+"F4.wireOp",EDGE,"E8.top"),sQuery(id+"F13.wireOp",EDGE,"E14"),sQuery(id+"F15.wireOp",EDGE,"E19"),sQuery(id+"F15.wireOp",EDGE,"E21")])]})]});
            var Q11;
            Q11=makeQuery(id+"F5.opExtrude","CAP_EDGE",EDGE,{"disambiguationData":[OSD([sQuery(id+"F4.wireOp",EDGE,"E8.top")])],"isStart":true});
            var Q12;
            Q12=makeQuery(id+"F18.boolean.opBoolean","MERGE",EDGE,{"derivedFrom":[makeQuery(id+"F14.boolean.opBoolean","MERGE",EDGE,{"derivedFrom":[makeQuery(id+"F5.opExtrude","CAP_EDGE",EDGE,{"disambiguationData":[OSD([sQuery(id+"F4.wireOp",EDGE,"E8.top")])],"isStart":false}),makeQuery(id+"F14.opExtrude","CAP_EDGE",EDGE,{"disambiguationData":[OSD([sQuery(id+"F13.wireOp",EDGE,"E14")])],"isStart":true})]}),makeQuery(id+"F18.opExtrude","CAP_EDGE",EDGE,{"disambiguationData":[OSD([sQuery(id+"F17.wireOp",EDGE,"E27.bottom")])],"isStart":true})]});
            var Q13;
            Q13=makeQuery(id+"F18.opExtrude","CAP_EDGE",EDGE,{"disambiguationData":[OSD([sQuery(id+"F17.wireOp",EDGE,"E27.bottom")])],"isStart":false});
            var Q14;
            Q14=makeQuery(id+"F18.opExtrude","SWEPT_EDGE",EDGE,{"disambiguationData":[OSD([sQuery(id+"F17.wireOp",EDGE,"E27.bottom"),sQuery(id+"F17.wireOp",EDGE,"E27.left")])]});
            fillet(context, id + "F28", {"entities" : qUnion([Q0, Q1, Q2, Q3, Q4, Q5, Q6, Q7, Q8, Q9, Q10, Q11, Q12, Q13, Q14]), "radius" : 3 * mm, "tangentPropagation" : true, "allowEdgeOverflow" : false});
        }
        {
            var Q0;
            Q0=makeQuery(id+"F5.boolean.opBoolean","SPLIT",EDGE,{"derivedFrom":makeQuery(id+"F5.opExtrude","CAP_EDGE",EDGE,{"disambiguationData":[OSD([sQuery(id+"F4.wireOp",EDGE,"E8.left")])],"isStart":true})});
            var Q1;
            Q1=makeQuery(id+"F22.opExtrude","SWEPT_EDGE",EDGE,{"disambiguationData":[OSD([sQuery(id+"F2.wireOp",EDGE,"E6"),sQuery(id+"F21.wireOp",EDGE,"E31")])]});
            var Q2;
            Q2=makeQuery(id+"F22.opExtrude","SWEPT_EDGE",EDGE,{"disambiguationData":[OSD([sQuery(id+"F2.wireOp",EDGE,"E5.bottom"),sQuery(id+"F2.wireOp",EDGE,"E7"),sQuery(id+"F21.wireOp",EDGE,"E31")])]});
            var Q3;
            Q3=makeQuery(id+"F22.opExtrude","CAP_EDGE",EDGE,{"disambiguationData":[OSD([sQuery(id+"F21.wireOp",EDGE,"E31")])],"isStart":false});
            var Q4;
            Q4=makeQuery(id+"F7.opExtrude","CAP_EDGE",EDGE,{"disambiguationData":[OSD([sQuery(id+"F6.wireOp",EDGE,"E9.bottom")])],"isStart":true});
            fillet(context, id + "F29", {"entities" : qUnion([Q0, Q1, Q2, Q3, Q4]), "radius" : 1.5 * mm, "tangentPropagation" : true, "allowEdgeOverflow" : false});
        }
        {
            var Q0;
            {var subQ0=sQuery(id+"F0.wireOp",EDGE,"E0.right");Q0=makeQuery(id+"F16.boolean.opBoolean","MERGE",FACE,{"derivedFrom":[makeQuery(id+"F12.opBoolean","MERGE",FACE,{"derivedFrom":[makeQuery(id+"F1.opExtrude","SWEPT_FACE",FACE,{"disambiguationData":[OSD([subQ0]),TDD([makeQuery(id+"F0.imprint","IMPRINT",EDGE,{"disambiguationData":[TD([[makeQuery(id+"F0.imprint","INTERSECT",VERTEX,{"derivedFrom":[sQuery(id+"F0.wireOp",EDGE,"E0.bottom"),subQ0]}),-1.0]])],"derivedFrom":subQ0})])]}),makeQuery(id+"F1.opExtrude","SWEPT_FACE",FACE,{"disambiguationData":[OSD([subQ0]),TDD([makeQuery(id+"F0.imprint","IMPRINT",EDGE,{"disambiguationData":[TD([[makeQuery(id+"F0.imprint","INTERSECT",VERTEX,{"derivedFrom":[sQuery(id+"F0.wireOp",EDGE,"E0.top"),subQ0]}),1.0]])],"derivedFrom":subQ0})])]}),makeQuery(id+"F3.opExtrude","SWEPT_FACE",FACE,{"disambiguationData":[OSD([sQuery(id+"F2.wireOp",EDGE,"E5.left")])]}),makeQuery(id+"F7.opExtrude","SWEPT_FACE",FACE,{"disambiguationData":[OSD([sQuery(id+"F6.wireOp",EDGE,"E9.left")])]}),makeQuery(id+"F9.opExtrude","SWEPT_FACE",FACE,{"disambiguationData":[OSD([sQuery(id+"F8.wireOp",EDGE,"E10.left")])]})]}),makeQuery(id+"F16.opExtrude","SWEPT_FACE",FACE,{"disambiguationData":[OSD([sQuery(id+"F15.wireOp",EDGE,"E20")])]})]});}
            cPlane(context, id + "F30", {"entities" : qUnion([Q0]), "cplaneType" : CPlaneType.OFFSET, "offset" : 10 * mm, "width" : 150 * mm, "height" : 150 * mm});
        }
        {
            var Q0;
            Q0=makeQuery(id+"F1.opExtrude","SWEPT_BODY",BODY,{"disambiguationData":[OSD([sQuery(id+"F0.wireOp",EDGE,"E0.bottom"),sQuery(id+"F0.wireOp",EDGE,"E0.left"),sQuery(id+"F0.wireOp",EDGE,"E0.right"),sQuery(id+"F0.wireOp",EDGE,"E3.bottom")])]});
            var Q1;
            Q1=qCreatedBy(id+"F30.planeOp",FACE);
            mirror(context, id + "F31", {"entities" : qUnion([Q0]), "mirrorPlane" : qUnion([Q1])});
        }
    });
